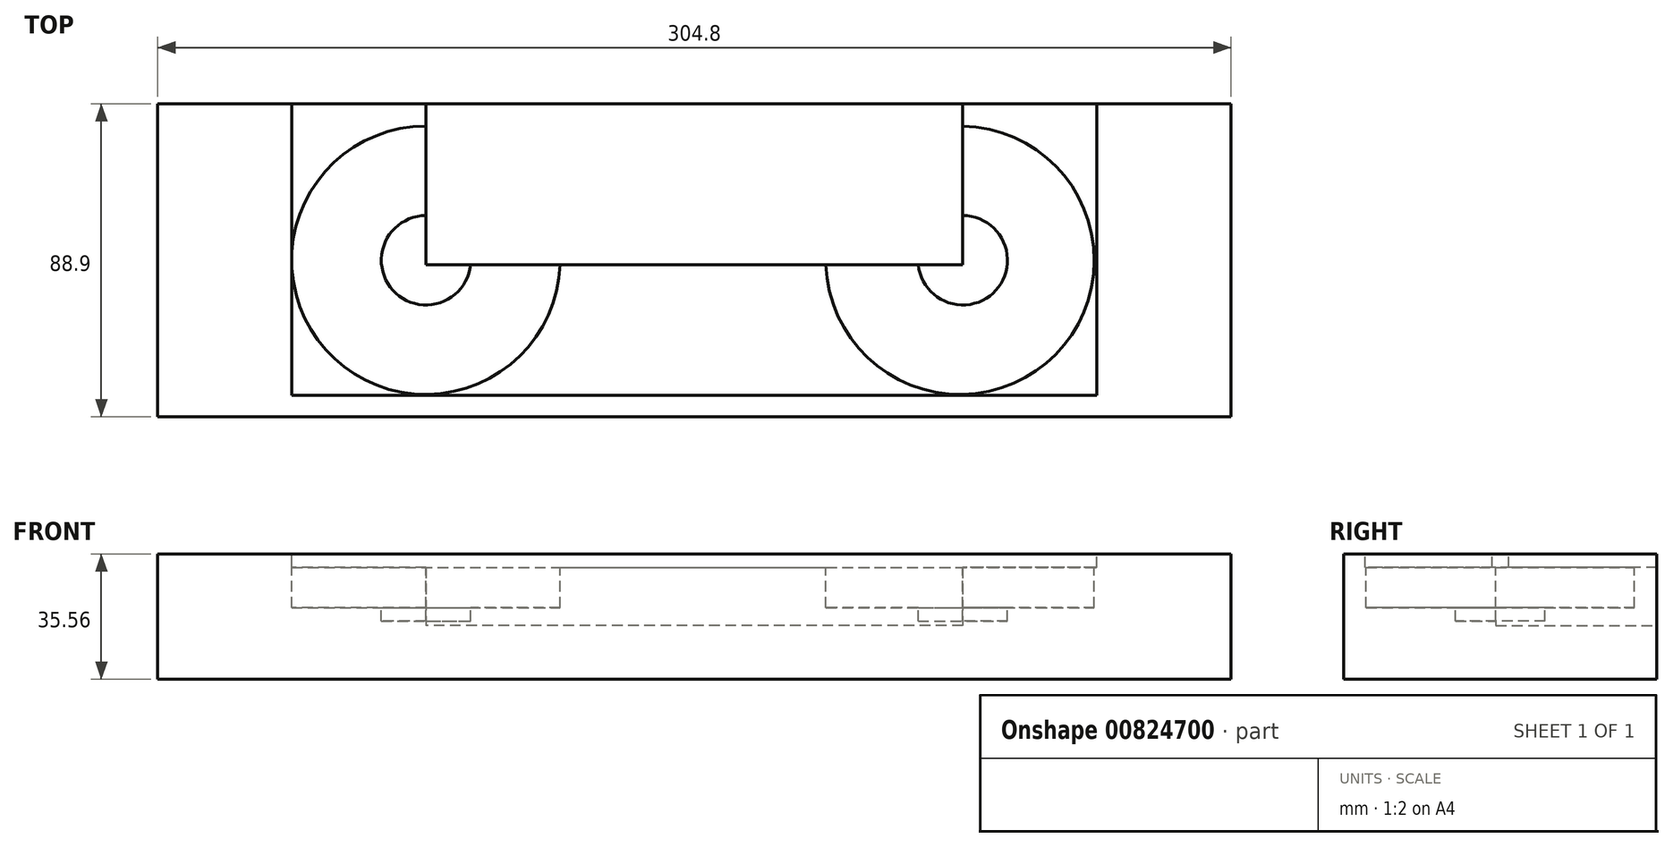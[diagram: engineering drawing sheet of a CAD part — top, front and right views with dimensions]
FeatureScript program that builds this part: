
annotation { "Feature Type Name" : "Feature", "Feature Type Description" : "" }
export const myFeature = defineFeature(function(context is Context, id is Id, definition is map)
    precondition{}
    {
        {
            var Q0;
            Q0=qCreatedBy(makeId("Top.planeOp"),FACE);
            var sketch = newSketch(context, id + "F0", { "sketchPlane" : qUnion([Q0])});
            skLineSegment(sketch, "E0.bottom", {"start": v(152.4, -44.45) * mm, "end": v(-152.4, -44.45) * mm});
            skLineSegment(sketch, "E0.top", {"start": v(152.4, 44.45) * mm, "end": v(-152.4, 44.45) * mm});
            skLineSegment(sketch, "E0.left", {"start": v(152.4, -44.45) * mm, "end": v(152.4, 44.45) * mm});
            skLineSegment(sketch, "E0.right", {"start": v(-152.4, -44.45) * mm, "end": v(-152.4, 44.45) * mm});
            skPoint(sketch, "E0.middle", {"position": v(0, 0) * mm});
            skSolve(sketch);
        }
        {
            var Q0;
            Q0 = qSketchRegion(id + "F0", true);
            extrude(context, id + "F1", {"entities" : qUnion([Q0]), "depth" : 35.56 * mm, "offsetDistance" : 25.4 * mm});
        }
        {
            var Q0;
            Q0=makeQuery(id+"F1.opExtrude","CAP_FACE",FACE,{"disambiguationData":[OSD([sQuery(id+"F0.wireOp",EDGE,"E0.bottom"),sQuery(id+"F0.wireOp",EDGE,"E0.top"),sQuery(id+"F0.wireOp",EDGE,"E0.left"),sQuery(id+"F0.wireOp",EDGE,"E0.right")])],"isStart":false});
            var sketch = newSketch(context, id + "F2", { "sketchPlane" : qUnion([Q0])});
            skCircle(sketch, "E1", {"center": v(75.44, 0) * mm, "radius": 38.1 * mm});
            skSolve(sketch);
        }
        {
            var Q0;
            Q0 = qSketchRegion(id + "F2", true);
            extrude(context, id + "F3", {"entities" : qUnion([Q0]), "operationType" : NewBodyOperationType.REMOVE, "oppositeDirection" : true, "depth" : 15.24 * mm, "offsetDistance" : 25.4 * mm});
        }
        {
            var Q0;
            Q0=makeQuery(id+"F1.opExtrude","CAP_FACE",FACE,{"disambiguationData":[OSD([sQuery(id+"F0.wireOp",EDGE,"E0.bottom"),sQuery(id+"F0.wireOp",EDGE,"E0.top"),sQuery(id+"F0.wireOp",EDGE,"E0.left"),sQuery(id+"F0.wireOp",EDGE,"E0.right")])],"isStart":false});
            var sketch = newSketch(context, id + "F4", { "sketchPlane" : qUnion([Q0])});
            skCircle(sketch, "E2", {"center": v(-76.27, 0) * mm, "radius": 38.1 * mm});
            skSolve(sketch);
        }
        {
            var Q0;
            Q0 = qSketchRegion(id + "F4", true);
            extrude(context, id + "F5", {"entities" : qUnion([Q0]), "operationType" : NewBodyOperationType.REMOVE, "oppositeDirection" : true, "depth" : 15.24 * mm, "offsetDistance" : 25.4 * mm});
        }
        {
            var Q0;
            Q0=makeQuery(id+"F1.opExtrude","SWEPT_FACE",FACE,{"disambiguationData":[OSD([sQuery(id+"F0.wireOp",EDGE,"E0.top")])]});
            var sketch = newSketch(context, id + "F6", { "sketchPlane" : qUnion([Q0])});
            skLineSegment(sketch, "E3.bottom", {"start": v(-76.2, 35.56) * mm, "end": v(76.2, 35.56) * mm});
            skLineSegment(sketch, "E3.top", {"start": v(-76.2, 15.24) * mm, "end": v(76.2, 15.24) * mm});
            skLineSegment(sketch, "E3.left", {"start": v(-76.2, 35.56) * mm, "end": v(-76.2, 15.24) * mm});
            skLineSegment(sketch, "E3.right", {"start": v(76.2, 35.56) * mm, "end": v(76.2, 15.24) * mm});
            skPoint(sketch, "E3.middle", {"position": v(0, 25.4) * mm});
            skSolve(sketch);
        }
        {
            var Q0;
            Q0 = qSketchRegion(id + "F6", true);
            extrude(context, id + "F7", {"entities" : qUnion([Q0]), "operationType" : NewBodyOperationType.REMOVE, "oppositeDirection" : true, "depth" : 45.72 * mm, "offsetDistance" : 25.4 * mm});
        }
        {
            var Q0;
            Q0=makeQuery(id+"F1.opExtrude","CAP_FACE",FACE,{"disambiguationData":[OSD([sQuery(id+"F0.wireOp",EDGE,"E0.bottom"),sQuery(id+"F0.wireOp",EDGE,"E0.top"),sQuery(id+"F0.wireOp",EDGE,"E0.left"),sQuery(id+"F0.wireOp",EDGE,"E0.right")])],"isStart":false});
            var sketch = newSketch(context, id + "F8", { "sketchPlane" : qUnion([Q0])});
            skPoint(sketch, "E4.oppositeSnap0", {"position": v(114.3, 44.45) * mm});
            skLineSegment(sketch, "E4.bottom", {"start": v(-114.3, 44.45) * mm, "end": v(114.3, 44.45) * mm});
            skLineSegment(sketch, "E4.top", {"start": v(-114.3, -38.34) * mm, "end": v(114.3, -38.34) * mm});
            skLineSegment(sketch, "E4.left", {"start": v(-114.3, 44.45) * mm, "end": v(-114.3, -38.34) * mm});
            skLineSegment(sketch, "E4.right", {"start": v(114.3, 44.45) * mm, "end": v(114.3, -38.34) * mm});
            skSolve(sketch);
        }
        {
            var Q0;
            Q0 = qSketchRegion(id + "F8", true);
            extrude(context, id + "F9", {"entities" : qUnion([Q0]), "operationType" : NewBodyOperationType.REMOVE, "oppositeDirection" : true, "depth" : 3.8 * mm, "offsetDistance" : 25.4 * mm});
        }
        {
            var Q0;
            Q0=makeQuery(id+"F5.boolean.opBoolean","COPY",FACE,{"derivedFrom":makeQuery(id+"F5.opExtrude","CAP_FACE",FACE,{"disambiguationData":[OSD([sQuery(id+"F4.wireOp",EDGE,"E2")])],"isStart":false})});
            var sketch = newSketch(context, id + "F10", { "sketchPlane" : qUnion([Q0])});
            skCircle(sketch, "E5", {"center": v(-76.2, 0) * mm, "radius": 12.7 * mm});
            skSolve(sketch);
        }
        {
            var Q0;
            Q0 = qSketchRegion(id + "F10", true);
            extrude(context, id + "F11", {"entities" : qUnion([Q0]), "operationType" : NewBodyOperationType.REMOVE, "oppositeDirection" : true, "depth" : 3.8 * mm, "offsetDistance" : 25.4 * mm});
        }
        {
            var Q0;
            Q0=makeQuery(id+"F3.boolean.opBoolean","COPY",FACE,{"derivedFrom":makeQuery(id+"F3.opExtrude","CAP_FACE",FACE,{"disambiguationData":[OSD([sQuery(id+"F2.wireOp",EDGE,"E1")])],"isStart":false})});
            var sketch = newSketch(context, id + "F12", { "sketchPlane" : qUnion([Q0])});
            skCircle(sketch, "E6", {"center": v(76.2, 0) * mm, "radius": 12.7 * mm});
            skSolve(sketch);
        }
        {
            var Q0;
            Q0 = qSketchRegion(id + "F12", true);
            extrude(context, id + "F13", {"entities" : qUnion([Q0]), "operationType" : NewBodyOperationType.REMOVE, "oppositeDirection" : true, "depth" : 3.8 * mm, "offsetDistance" : 25.4 * mm});
        }
        {
            var Q0;
            {var subQ1=sQuery(id+"F8.wireOp",EDGE,"E4.right");var subQ2=sQuery(id+"F8.wireOp",EDGE,"E4.top");var subQ3=sQuery(id+"F8.wireOp",EDGE,"E4.left");Q0=makeQuery(id+"F9.boolean.opBoolean","COPY",FACE,{"disambiguationData":[TD([makeQuery(id+"F3.boolean.opBoolean","COPY",FACE,{"derivedFrom":makeQuery(id+"F3.opExtrude","SWEPT_FACE",FACE,{"disambiguationData":[OSD([sQuery(id+"F2.wireOp",EDGE,"E1")])]})})])],"derivedFrom":makeQuery(id+"F9.opExtrude","CAP_FACE",FACE,{"disambiguationData":[OSD([sQuery(id+"F8.wireOp",EDGE,"E4.bottom"),subQ2,subQ3,subQ1])],"isStart":false})});}
            var sketch = newSketch(context, id + "F14", { "sketchPlane" : qUnion([Q0])});
            skLineSegment(sketch, "E7.bottom", {"start": v(-42.62, 0) * mm, "end": v(41.2, 0) * mm});
            skLineSegment(sketch, "E7.top", {"start": v(-42.62, -16.7) * mm, "end": v(41.2, -16.7) * mm});
            skLineSegment(sketch, "E7.left", {"start": v(-42.62, 0) * mm, "end": v(-42.62, -16.7) * mm});
            skLineSegment(sketch, "E7.right", {"start": v(41.2, 0) * mm, "end": v(41.2, -16.7) * mm});
            skSolve(sketch);
        }
        {
            var Q0;
            {var subQ0=sQuery(id+"F14.wireOp",EDGE,"E7.bottom");var subQ1=makeQuery(id+"F9.opExtrude","CAP_FACE",FACE,{"disambiguationData":[OSD([sQuery(id+"F8.wireOp",EDGE,"E4.bottom"),sQuery(id+"F8.wireOp",EDGE,"E4.top"),sQuery(id+"F8.wireOp",EDGE,"E4.left"),sQuery(id+"F8.wireOp",EDGE,"E4.right")])],"isStart":false});var subQ2=makeQuery(id+"F9.boolean.opBoolean","INTERSECT",EDGE,{"disambiguationData":[OD(0.0)],"derivedFrom":[makeQuery(id+"F5.boolean.opBoolean","COPY",FACE,{"derivedFrom":makeQuery(id+"F5.opExtrude","SWEPT_FACE",FACE,{"disambiguationData":[OSD([sQuery(id+"F4.wireOp",EDGE,"E2")])]})}),subQ1]});var subQ3=makeQuery(id+"F14.imprint","INTERSECT",VERTEX,{"derivedFrom":[subQ2,subQ0]});Q0=makeQuery(id+"F14.imprint","IMPRINT",FACE,{"disambiguationData":[TD([[makeQuery(id+"F14.imprint","IMPRINT",EDGE,{"disambiguationData":[TD([[subQ3,-1.0]])],"derivedFrom":subQ0}),-1.0]])]});}
            extrude(context, id + "F15", {"entities" : qUnion([Q0]), "operationType" : NewBodyOperationType.REMOVE, "oppositeDirection" : true, "depth" : 6.35 * mm, "offsetDistance" : 25.4 * mm});
        }
    });
